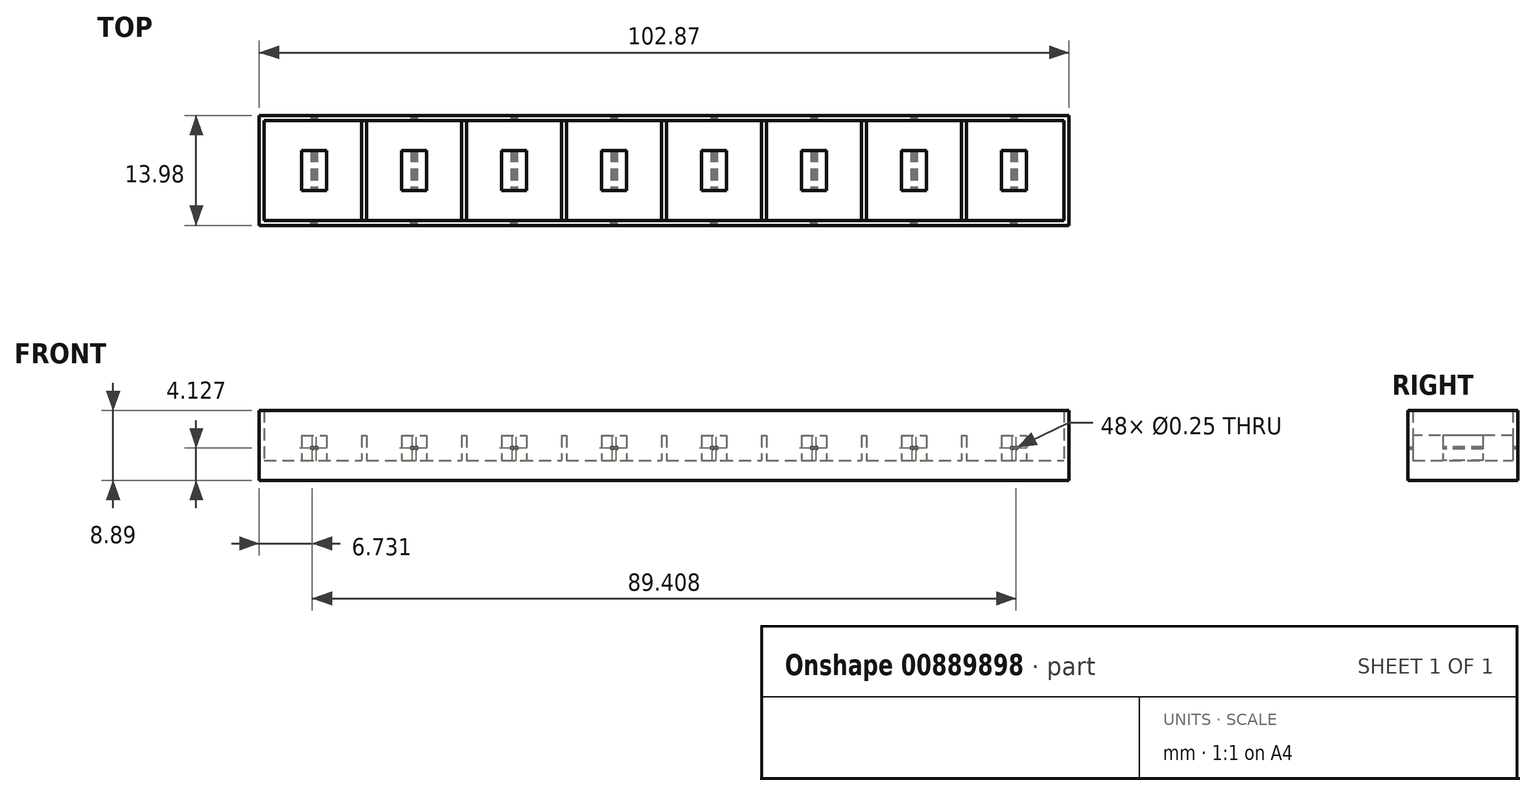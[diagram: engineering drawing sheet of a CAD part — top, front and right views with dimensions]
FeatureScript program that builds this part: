
annotation { "Feature Type Name" : "Feature", "Feature Type Description" : "" }
export const myFeature = defineFeature(function(context is Context, id is Id, definition is map)
    precondition{}
    {
        {
            var Q0;
            Q0=qCreatedBy(makeId("Top.planeOp"),FACE);
            var sketch = newSketch(context, id + "F0", { "sketchPlane" : qUnion([Q0])});
            skLineSegment(sketch, "E0.bottom", {"start": v(-32.74, 0) * mm, "end": v(68.86, 0) * mm});
            skLineSegment(sketch, "E0.top", {"start": v(-32.74, 12.7) * mm, "end": v(68.86, 12.7) * mm});
            skLineSegment(sketch, "E0.left", {"start": v(-32.74, 0) * mm, "end": v(-32.74, 12.7) * mm});
            skLineSegment(sketch, "E0.right", {"start": v(68.86, 0) * mm, "end": v(68.86, 12.7) * mm});
            skLineSegment(sketch, "E1.bottom", {"start": v(69.5, 13.34) * mm, "end": v(-33.37, 13.33) * mm});
            skLineSegment(sketch, "E1.top", {"start": v(69.5, -0.63) * mm, "end": v(-33.37, -0.64) * mm});
            skLineSegment(sketch, "E1.left", {"start": v(69.5, 13.34) * mm, "end": v(69.5, -0.63) * mm});
            skLineSegment(sketch, "E1.right", {"start": v(-33.37, 13.33) * mm, "end": v(-33.37, -0.64) * mm});
            skLineSegment(sketch, "E2.MirrorCS", {"start": v(5.68, 0) * mm, "end": v(5.68, 12.7) * mm});
            skLineSegment(sketch, "E3.MirrorCS", {"start": v(5.04, 0) * mm, "end": v(5.04, 12.7) * mm});
            skLineSegment(sketch, "E4.MirrorCS", {"start": v(-7.02, 0) * mm, "end": v(-7.02, 12.7) * mm});
            skLineSegment(sketch, "E5.MirrorCS", {"start": v(-7.66, 0) * mm, "end": v(-7.66, 12.7) * mm});
            skLineSegment(sketch, "E6.MirrorCS", {"start": v(-19.72, 0) * mm, "end": v(-19.72, 12.7) * mm});
            skLineSegment(sketch, "E7", {"start": v(-20.36, 12.7) * mm, "end": v(-20.36, 0) * mm});
            skLineSegment(sketch, "E8.MirrorCS", {"start": v(30.44, 0) * mm, "end": v(30.44, 12.7) * mm});
            skLineSegment(sketch, "E9.MirrorCS", {"start": v(31.08, 0) * mm, "end": v(31.08, 12.7) * mm});
            skLineSegment(sketch, "E10.MirrorCS", {"start": v(43.14, 0) * mm, "end": v(43.14, 12.7) * mm});
            skLineSegment(sketch, "E11.MirrorCS", {"start": v(43.78, 0) * mm, "end": v(43.78, 12.7) * mm});
            skLineSegment(sketch, "E12.MirrorCS", {"start": v(55.84, 0) * mm, "end": v(55.84, 12.7) * mm});
            skLineSegment(sketch, "E13.MirrorCS", {"start": v(56.48, 12.7) * mm, "end": v(56.48, 0) * mm});
            skLineSegment(sketch, "E14", {"start": v(17.74, 12.7) * mm, "end": v(17.74, 0) * mm});
            skLineSegment(sketch, "E15", {"start": v(18.38, 0) * mm, "end": v(18.38, 12.7) * mm});
            skLineSegment(sketch, "E16.MirrorCS", {"start": v(-24.8, 8.9) * mm, "end": v(-24.8, 3.8) * mm});
            skLineSegment(sketch, "E17.MirrorCS", {"start": v(-27.97, 8.89) * mm, "end": v(-27.97, 3.8) * mm});
            skLineSegment(sketch, "E18", {"start": v(-27.97, 8.89) * mm, "end": v(-24.8, 8.9) * mm});
            skLineSegment(sketch, "E19", {"start": v(-27.97, 3.8) * mm, "end": v(-24.8, 3.8) * mm});
            skLineSegment(sketch, "E20.1.0.0", {"start": v(-15.27, 8.89) * mm, "end": v(-12.1, 8.9) * mm});
            skLineSegment(sketch, "E20.1.0.1", {"start": v(-12.1, 8.9) * mm, "end": v(-12.1, 3.8) * mm});
            skLineSegment(sketch, "E20.1.0.2", {"start": v(-15.27, 8.89) * mm, "end": v(-15.27, 3.8) * mm});
            skLineSegment(sketch, "E20.1.0.3", {"start": v(-15.27, 3.8) * mm, "end": v(-12.1, 3.8) * mm});
            skLineSegment(sketch, "E20.2.0.0", {"start": v(-2.57, 8.89) * mm, "end": v(0.6, 8.9) * mm});
            skLineSegment(sketch, "E20.2.0.1", {"start": v(0.6, 8.9) * mm, "end": v(0.6, 3.8) * mm});
            skLineSegment(sketch, "E20.2.0.2", {"start": v(-2.57, 8.89) * mm, "end": v(-2.57, 3.8) * mm});
            skLineSegment(sketch, "E20.2.0.3", {"start": v(-2.57, 3.8) * mm, "end": v(0.6, 3.8) * mm});
            skLineSegment(sketch, "E20.3.0.0", {"start": v(10.13, 8.89) * mm, "end": v(13.3, 8.9) * mm});
            skLineSegment(sketch, "E20.3.0.1", {"start": v(13.3, 8.9) * mm, "end": v(13.3, 3.8) * mm});
            skLineSegment(sketch, "E20.3.0.2", {"start": v(10.13, 8.89) * mm, "end": v(10.13, 3.8) * mm});
            skLineSegment(sketch, "E20.3.0.3", {"start": v(10.13, 3.8) * mm, "end": v(13.3, 3.8) * mm});
            skLineSegment(sketch, "E20.4.0.0", {"start": v(22.83, 8.89) * mm, "end": v(26, 8.9) * mm});
            skLineSegment(sketch, "E20.4.0.1", {"start": v(26, 8.9) * mm, "end": v(26, 3.8) * mm});
            skLineSegment(sketch, "E20.4.0.2", {"start": v(22.83, 8.89) * mm, "end": v(22.83, 3.8) * mm});
            skLineSegment(sketch, "E20.4.0.3", {"start": v(22.83, 3.8) * mm, "end": v(26, 3.8) * mm});
            skLineSegment(sketch, "E20.5.0.0", {"start": v(35.53, 8.89) * mm, "end": v(38.7, 8.9) * mm});
            skLineSegment(sketch, "E20.5.0.1", {"start": v(38.7, 8.9) * mm, "end": v(38.7, 3.8) * mm});
            skLineSegment(sketch, "E20.5.0.2", {"start": v(35.53, 8.89) * mm, "end": v(35.53, 3.8) * mm});
            skLineSegment(sketch, "E20.5.0.3", {"start": v(35.53, 3.8) * mm, "end": v(38.7, 3.8) * mm});
            skLineSegment(sketch, "E20.6.0.0", {"start": v(48.23, 8.89) * mm, "end": v(51.4, 8.9) * mm});
            skLineSegment(sketch, "E20.6.0.1", {"start": v(51.4, 8.9) * mm, "end": v(51.4, 3.8) * mm});
            skLineSegment(sketch, "E20.6.0.2", {"start": v(48.23, 8.89) * mm, "end": v(48.23, 3.8) * mm});
            skLineSegment(sketch, "E20.6.0.3", {"start": v(48.23, 3.8) * mm, "end": v(51.4, 3.8) * mm});
            skLineSegment(sketch, "E20.7.0.0", {"start": v(60.93, 8.89) * mm, "end": v(64.1, 8.9) * mm});
            skLineSegment(sketch, "E20.7.0.1", {"start": v(64.1, 8.9) * mm, "end": v(64.1, 3.8) * mm});
            skLineSegment(sketch, "E20.7.0.2", {"start": v(60.93, 8.89) * mm, "end": v(60.93, 3.8) * mm});
            skLineSegment(sketch, "E20.7.0.3", {"start": v(60.93, 3.8) * mm, "end": v(64.1, 3.8) * mm});
            skLineSegment(sketch, "E20.direction1", {"start": v(-27.97, 3.8) * mm, "end": v(-15.27, 3.8) * mm, "construction": true});
            skSolve(sketch);
        }
        {
            var Q0;
            {var subQ1=sQuery(id+"F0.wireOp",EDGE,"E5.MirrorCS");Q0=makeQuery(id+"F0.imprint","IMPRINT",FACE,{"disambiguationData":[TD([[makeQuery(id+"F0.imprint","IMPRINT",EDGE,{"derivedFrom":subQ1}),1.0]])]});}
            var Q1;
            {var subQ1=sQuery(id+"F0.wireOp",EDGE,"E3.MirrorCS");Q1=makeQuery(id+"F0.imprint","IMPRINT",FACE,{"disambiguationData":[TD([[makeQuery(id+"F0.imprint","IMPRINT",EDGE,{"derivedFrom":subQ1}),1.0]])]});}
            var Q2;
            {var subQ1=sQuery(id+"F0.wireOp",EDGE,"E0.right");Q2=makeQuery(id+"F0.imprint","IMPRINT",FACE,{"disambiguationData":[TD([[makeQuery(id+"F0.imprint","IMPRINT",EDGE,{"derivedFrom":subQ1}),1.0]])]});}
            var Q3;
            {var subQ1=sQuery(id+"F0.wireOp",EDGE,"E11.MirrorCS");Q3=makeQuery(id+"F0.imprint","IMPRINT",FACE,{"disambiguationData":[TD([[makeQuery(id+"F0.imprint","IMPRINT",EDGE,{"derivedFrom":subQ1}),-1.0]])]});}
            var Q4;
            {var subQ1=sQuery(id+"F0.wireOp",EDGE,"E0.left");Q4=makeQuery(id+"F0.imprint","IMPRINT",FACE,{"disambiguationData":[TD([[makeQuery(id+"F0.imprint","IMPRINT",EDGE,{"derivedFrom":subQ1}),-1.0]])]});}
            var Q5;
            Q5=makeQuery(id+"F0.imprint","IMPRINT",FACE,{"disambiguationData":[TD([[makeQuery(id+"F0.imprint","IMPRINT",EDGE,{"derivedFrom":sQuery(id+"F0.wireOp",EDGE,"E20.6.0.0")}),-1.0]])]});
            var Q6;
            Q6=makeQuery(id+"F0.imprint","IMPRINT",FACE,{"disambiguationData":[TD([[makeQuery(id+"F0.imprint","IMPRINT",EDGE,{"derivedFrom":sQuery(id+"F0.wireOp",EDGE,"E20.4.0.0")}),-1.0]])]});
            var Q7;
            Q7=makeQuery(id+"F0.imprint","IMPRINT",FACE,{"disambiguationData":[TD([[makeQuery(id+"F0.imprint","IMPRINT",EDGE,{"derivedFrom":sQuery(id+"F0.wireOp",EDGE,"E16.MirrorCS")}),-1.0]])]});
            var Q8;
            Q8=makeQuery(id+"F0.imprint","IMPRINT",FACE,{"disambiguationData":[TD([[makeQuery(id+"F0.imprint","IMPRINT",EDGE,{"derivedFrom":sQuery(id+"F0.wireOp",EDGE,"E20.2.0.0")}),-1.0]])]});
            var Q9;
            Q9=makeQuery(id+"F0.imprint","IMPRINT",FACE,{"disambiguationData":[TD([[makeQuery(id+"F0.imprint","IMPRINT",EDGE,{"derivedFrom":sQuery(id+"F0.wireOp",EDGE,"E20.1.0.0")}),-1.0]])]});
            var Q10;
            Q10=makeQuery(id+"F0.imprint","IMPRINT",FACE,{"disambiguationData":[TD([[makeQuery(id+"F0.imprint","IMPRINT",EDGE,{"derivedFrom":sQuery(id+"F0.wireOp",EDGE,"E20.7.0.0")}),-1.0]])]});
            var Q11;
            {var subQ1=sQuery(id+"F0.wireOp",EDGE,"E9.MirrorCS");Q11=makeQuery(id+"F0.imprint","IMPRINT",FACE,{"disambiguationData":[TD([[makeQuery(id+"F0.imprint","IMPRINT",EDGE,{"derivedFrom":subQ1}),-1.0]])]});}
            var Q12;
            Q12=makeQuery(id+"F0.imprint","IMPRINT",FACE,{"disambiguationData":[TD([[makeQuery(id+"F0.imprint","IMPRINT",EDGE,{"derivedFrom":sQuery(id+"F0.wireOp",EDGE,"E20.3.0.0")}),-1.0]])]});
            var Q13;
            {var subQ1=sQuery(id+"F0.wireOp",EDGE,"E2.MirrorCS");Q13=makeQuery(id+"F0.imprint","IMPRINT",FACE,{"disambiguationData":[TD([[makeQuery(id+"F0.imprint","IMPRINT",EDGE,{"derivedFrom":subQ1}),-1.0]])]});}
            var Q14;
            {var subQ1=sQuery(id+"F0.wireOp",EDGE,"E8.MirrorCS");Q14=makeQuery(id+"F0.imprint","IMPRINT",FACE,{"disambiguationData":[TD([[makeQuery(id+"F0.imprint","IMPRINT",EDGE,{"derivedFrom":subQ1}),1.0]])]});}
            var Q15;
            Q15=makeQuery(id+"F0.imprint","IMPRINT",FACE,{"disambiguationData":[TD([[makeQuery(id+"F0.imprint","IMPRINT",EDGE,{"derivedFrom":sQuery(id+"F0.wireOp",EDGE,"E20.5.0.0")}),-1.0]])]});
            var Q16;
            {var subQ15=sQuery(id+"F0.wireOp",EDGE,"E0.left");Q16=makeQuery(id+"F0.imprint","IMPRINT",FACE,{"disambiguationData":[TD([[makeQuery(id+"F0.imprint","IMPRINT",EDGE,{"derivedFrom":subQ15}),1.0]])]});}
            var Q17;
            {var subQ0=sQuery(id+"F0.wireOp",EDGE,"E2.MirrorCS");Q17=makeQuery(id+"F0.imprint","IMPRINT",FACE,{"disambiguationData":[TD([[makeQuery(id+"F0.imprint","IMPRINT",EDGE,{"derivedFrom":subQ0}),1.0]])]});}
            var Q18;
            {var subQ0=sQuery(id+"F0.wireOp",EDGE,"E12.MirrorCS");Q18=makeQuery(id+"F0.imprint","IMPRINT",FACE,{"disambiguationData":[TD([[makeQuery(id+"F0.imprint","IMPRINT",EDGE,{"derivedFrom":subQ0}),-1.0]])]});}
            var Q19;
            {var subQ0=sQuery(id+"F0.wireOp",EDGE,"E14");Q19=makeQuery(id+"F0.imprint","IMPRINT",FACE,{"disambiguationData":[TD([[makeQuery(id+"F0.imprint","IMPRINT",EDGE,{"derivedFrom":subQ0}),1.0]])]});}
            var Q20;
            {var subQ0=sQuery(id+"F0.wireOp",EDGE,"E8.MirrorCS");Q20=makeQuery(id+"F0.imprint","IMPRINT",FACE,{"disambiguationData":[TD([[makeQuery(id+"F0.imprint","IMPRINT",EDGE,{"derivedFrom":subQ0}),-1.0]])]});}
            var Q21;
            {var subQ0=sQuery(id+"F0.wireOp",EDGE,"E10.MirrorCS");Q21=makeQuery(id+"F0.imprint","IMPRINT",FACE,{"disambiguationData":[TD([[makeQuery(id+"F0.imprint","IMPRINT",EDGE,{"derivedFrom":subQ0}),-1.0]])]});}
            var Q22;
            {var subQ0=sQuery(id+"F0.wireOp",EDGE,"E4.MirrorCS");Q22=makeQuery(id+"F0.imprint","IMPRINT",FACE,{"disambiguationData":[TD([[makeQuery(id+"F0.imprint","IMPRINT",EDGE,{"derivedFrom":subQ0}),1.0]])]});}
            var Q23;
            {var subQ0=sQuery(id+"F0.wireOp",EDGE,"E6.MirrorCS");Q23=makeQuery(id+"F0.imprint","IMPRINT",FACE,{"disambiguationData":[TD([[makeQuery(id+"F0.imprint","IMPRINT",EDGE,{"derivedFrom":subQ0}),1.0]])]});}
            extrude(context, id + "F1", {"entities" : qUnion([Q0, Q1, Q2, Q3, Q4, Q5, Q6, Q7, Q8, Q9, Q10, Q11, Q12, Q13, Q14, Q15, Q16, Q17, Q18, Q19, Q20, Q21, Q22, Q23]), "oppositeDirection" : true, "depth" : 2.54 * mm, "offsetDistance" : 25.4 * mm});
        }
        {
            var Q0;
            {var subQ19=sQuery(id+"F0.wireOp",EDGE,"E0.left");Q0=makeQuery(id+"F0.imprint","IMPRINT",FACE,{"disambiguationData":[TD([[makeQuery(id+"F0.imprint","IMPRINT",EDGE,{"derivedFrom":subQ19}),1.0]])]});}
            extrude(context, id + "F2", {"entities" : qUnion([Q0]), "operationType" : NewBodyOperationType.ADD, "depth" : 6.35 * mm, "offsetDistance" : 25.4 * mm});
        }
        {
            var Q0;
            Q0=makeQuery(id+"F0.imprint","IMPRINT",FACE,{"disambiguationData":[TD([[makeQuery(id+"F0.imprint","IMPRINT",EDGE,{"derivedFrom":sQuery(id+"F0.wireOp",EDGE,"E16.MirrorCS")}),-1.0]])]});
            var Q1;
            Q1=makeQuery(id+"F0.imprint","IMPRINT",FACE,{"disambiguationData":[TD([[makeQuery(id+"F0.imprint","IMPRINT",EDGE,{"derivedFrom":sQuery(id+"F0.wireOp",EDGE,"E20.1.0.0")}),-1.0]])]});
            var Q2;
            Q2=makeQuery(id+"F0.imprint","IMPRINT",FACE,{"disambiguationData":[TD([[makeQuery(id+"F0.imprint","IMPRINT",EDGE,{"derivedFrom":sQuery(id+"F0.wireOp",EDGE,"E20.2.0.0")}),-1.0]])]});
            var Q3;
            Q3=makeQuery(id+"F0.imprint","IMPRINT",FACE,{"disambiguationData":[TD([[makeQuery(id+"F0.imprint","IMPRINT",EDGE,{"derivedFrom":sQuery(id+"F0.wireOp",EDGE,"E20.3.0.0")}),-1.0]])]});
            var Q4;
            Q4=makeQuery(id+"F0.imprint","IMPRINT",FACE,{"disambiguationData":[TD([[makeQuery(id+"F0.imprint","IMPRINT",EDGE,{"derivedFrom":sQuery(id+"F0.wireOp",EDGE,"E20.4.0.0")}),-1.0]])]});
            var Q5;
            Q5=makeQuery(id+"F0.imprint","IMPRINT",FACE,{"disambiguationData":[TD([[makeQuery(id+"F0.imprint","IMPRINT",EDGE,{"derivedFrom":sQuery(id+"F0.wireOp",EDGE,"E20.5.0.0")}),-1.0]])]});
            var Q6;
            Q6=makeQuery(id+"F0.imprint","IMPRINT",FACE,{"disambiguationData":[TD([[makeQuery(id+"F0.imprint","IMPRINT",EDGE,{"derivedFrom":sQuery(id+"F0.wireOp",EDGE,"E20.6.0.0")}),-1.0]])]});
            var Q7;
            Q7=makeQuery(id+"F0.imprint","IMPRINT",FACE,{"disambiguationData":[TD([[makeQuery(id+"F0.imprint","IMPRINT",EDGE,{"derivedFrom":sQuery(id+"F0.wireOp",EDGE,"E20.7.0.0")}),-1.0]])]});
            var Q8;
            {var subQ0=sQuery(id+"F0.wireOp",EDGE,"E12.MirrorCS");Q8=makeQuery(id+"F0.imprint","IMPRINT",FACE,{"disambiguationData":[TD([[makeQuery(id+"F0.imprint","IMPRINT",EDGE,{"derivedFrom":subQ0}),-1.0]])]});}
            var Q9;
            {var subQ0=sQuery(id+"F0.wireOp",EDGE,"E10.MirrorCS");Q9=makeQuery(id+"F0.imprint","IMPRINT",FACE,{"disambiguationData":[TD([[makeQuery(id+"F0.imprint","IMPRINT",EDGE,{"derivedFrom":subQ0}),-1.0]])]});}
            var Q10;
            {var subQ0=sQuery(id+"F0.wireOp",EDGE,"E8.MirrorCS");Q10=makeQuery(id+"F0.imprint","IMPRINT",FACE,{"disambiguationData":[TD([[makeQuery(id+"F0.imprint","IMPRINT",EDGE,{"derivedFrom":subQ0}),-1.0]])]});}
            var Q11;
            {var subQ0=sQuery(id+"F0.wireOp",EDGE,"E14");Q11=makeQuery(id+"F0.imprint","IMPRINT",FACE,{"disambiguationData":[TD([[makeQuery(id+"F0.imprint","IMPRINT",EDGE,{"derivedFrom":subQ0}),1.0]])]});}
            var Q12;
            {var subQ0=sQuery(id+"F0.wireOp",EDGE,"E2.MirrorCS");Q12=makeQuery(id+"F0.imprint","IMPRINT",FACE,{"disambiguationData":[TD([[makeQuery(id+"F0.imprint","IMPRINT",EDGE,{"derivedFrom":subQ0}),1.0]])]});}
            var Q13;
            {var subQ0=sQuery(id+"F0.wireOp",EDGE,"E4.MirrorCS");Q13=makeQuery(id+"F0.imprint","IMPRINT",FACE,{"disambiguationData":[TD([[makeQuery(id+"F0.imprint","IMPRINT",EDGE,{"derivedFrom":subQ0}),1.0]])]});}
            var Q14;
            {var subQ0=sQuery(id+"F0.wireOp",EDGE,"E6.MirrorCS");Q14=makeQuery(id+"F0.imprint","IMPRINT",FACE,{"disambiguationData":[TD([[makeQuery(id+"F0.imprint","IMPRINT",EDGE,{"derivedFrom":subQ0}),1.0]])]});}
            extrude(context, id + "F3", {"entities" : qUnion([Q0, Q1, Q2, Q3, Q4, Q5, Q6, Q7, Q8, Q9, Q10, Q11, Q12, Q13, Q14]), "operationType" : NewBodyOperationType.ADD, "depth" : 3.17 * mm, "offsetDistance" : 25.4 * mm});
        }
        {
            var Q0;
            Q0=makeQuery(id+"F2.opExtrude","SWEPT_FACE",FACE,{"disambiguationData":[OSD([sQuery(id+"F0.wireOp",EDGE,"E0.bottom"),sQuery(id+"F0.wireOp",EDGE,"Ld5J9Fpd-gWnr-y3Wp-gADY-ncH7xOH5REKi.bottom")])]});
            var sketch = newSketch(context, id + "F4", { "sketchPlane" : qUnion([Q0])});
            skPoint(sketch, "E21", {"position": v(-24.67, 1.59) * mm});
            skPoint(sketch, "E22", {"position": v(-24.16, 1.59) * mm});
            skPoint(sketch, "E23.MirrorP", {"position": v(-36.86, 1.59) * mm});
            skPoint(sketch, "E24.MirrorP", {"position": v(-37.37, 1.59) * mm});
            skPoint(sketch, "E25.MirrorP", {"position": v(-49.56, 1.59) * mm});
            skPoint(sketch, "E26.MirrorP", {"position": v(-50.07, 1.59) * mm});
            skPoint(sketch, "E27.MirrorP", {"position": v(-62.26, 1.59) * mm});
            skPoint(sketch, "E28.MirrorP", {"position": v(-62.77, 1.59) * mm});
            skPoint(sketch, "E29.MirrorP", {"position": v(-11.97, 1.59) * mm});
            skPoint(sketch, "E30.MirrorP", {"position": v(-11.46, 1.59) * mm});
            skPoint(sketch, "E31.MirrorP", {"position": v(0.73, 1.59) * mm});
            skPoint(sketch, "E32.MirrorP", {"position": v(1.24, 1.59) * mm});
            skPoint(sketch, "E33.MirrorP", {"position": v(13.43, 1.59) * mm});
            skPoint(sketch, "E34.MirrorP", {"position": v(13.94, 1.59) * mm});
            skPoint(sketch, "E35.MirrorP", {"position": v(26.13, 1.59) * mm});
            skPoint(sketch, "E36.MirrorP", {"position": v(26.64, 1.59) * mm});
            skSolve(sketch);
        }
        {
            var Q0;
            Q0=sQuery(id+"F4.wireOp",VERTEX,"E36.MirrorP");
            var Q1;
            Q1=sQuery(id+"F4.wireOp",VERTEX,"E35.MirrorP");
            var Q2;
            Q2=sQuery(id+"F4.wireOp",VERTEX,"E34.MirrorP");
            var Q3;
            Q3=sQuery(id+"F4.wireOp",VERTEX,"E33.MirrorP");
            var Q4;
            Q4=sQuery(id+"F4.wireOp",VERTEX,"E32.MirrorP");
            var Q5;
            Q5=sQuery(id+"F4.wireOp",VERTEX,"E31.MirrorP");
            var Q6;
            Q6=sQuery(id+"F4.wireOp",VERTEX,"E30.MirrorP");
            var Q7;
            Q7=sQuery(id+"F4.wireOp",VERTEX,"E29.MirrorP");
            var Q8;
            Q8=sQuery(id+"F4.wireOp",VERTEX,"E22");
            var Q9;
            Q9=sQuery(id+"F4.wireOp",VERTEX,"E21");
            var Q10;
            Q10=sQuery(id+"F4.wireOp",VERTEX,"E23.MirrorP");
            var Q11;
            Q11=sQuery(id+"F4.wireOp",VERTEX,"E24.MirrorP");
            var Q12;
            Q12=sQuery(id+"F4.wireOp",VERTEX,"E25.MirrorP");
            var Q13;
            Q13=sQuery(id+"F4.wireOp",VERTEX,"E26.MirrorP");
            var Q14;
            Q14=sQuery(id+"F4.wireOp",VERTEX,"E27.MirrorP");
            var Q15;
            Q15=sQuery(id+"F4.wireOp",VERTEX,"E28.MirrorP");
            var Q16;
            Q16=makeQuery(id+"F1.opExtrude","SWEPT_BODY",BODY,{"disambiguationData":[OSD([sQuery(id+"F0.wireOp",EDGE,"E1.bottom"),sQuery(id+"F0.wireOp",EDGE,"E1.top"),sQuery(id+"F0.wireOp",EDGE,"E1.left"),sQuery(id+"F0.wireOp",EDGE,"E1.right")])]});
            hole(context, id + "F5", {"style" : HoleStyle.SIMPLE, "endStyle" : HoleEndStyle.THROUGH, "holeDiameter" : 0.25 * mm, "majorDiameter" : 6.35 * mm, "isTappedThrough" : true, "tappedDepth" : 12.7 * mm, "tapClearance" : 3, "locations" : qUnion([Q0, Q1, Q2, Q3, Q4, Q5, Q6, Q7, Q8, Q9, Q10, Q11, Q12, Q13, Q14, Q15]), "scope" : qUnion([Q16])});
        }
        {
            var Q0;
            Q0=sQuery(id+"F4.wireOp",VERTEX,"E28.MirrorP");
            var Q1;
            Q1=sQuery(id+"F4.wireOp",VERTEX,"E27.MirrorP");
            var Q2;
            Q2=sQuery(id+"F4.wireOp",VERTEX,"E26.MirrorP");
            var Q3;
            Q3=sQuery(id+"F4.wireOp",VERTEX,"E25.MirrorP");
            var Q4;
            Q4=sQuery(id+"F4.wireOp",VERTEX,"E24.MirrorP");
            var Q5;
            Q5=sQuery(id+"F4.wireOp",VERTEX,"E23.MirrorP");
            var Q6;
            Q6=sQuery(id+"F4.wireOp",VERTEX,"E21");
            var Q7;
            Q7=sQuery(id+"F4.wireOp",VERTEX,"E22");
            var Q8;
            Q8=sQuery(id+"F4.wireOp",VERTEX,"E29.MirrorP");
            var Q9;
            Q9=sQuery(id+"F4.wireOp",VERTEX,"E30.MirrorP");
            var Q10;
            Q10=sQuery(id+"F4.wireOp",VERTEX,"E31.MirrorP");
            var Q11;
            Q11=sQuery(id+"F4.wireOp",VERTEX,"E32.MirrorP");
            var Q12;
            Q12=sQuery(id+"F4.wireOp",VERTEX,"E33.MirrorP");
            var Q13;
            Q13=sQuery(id+"F4.wireOp",VERTEX,"E34.MirrorP");
            var Q14;
            Q14=sQuery(id+"F4.wireOp",VERTEX,"E35.MirrorP");
            var Q15;
            Q15=sQuery(id+"F4.wireOp",VERTEX,"E36.MirrorP");
            var Q16;
            Q16=makeQuery(id+"F1.opExtrude","SWEPT_BODY",BODY,{"disambiguationData":[OSD([sQuery(id+"F0.wireOp",EDGE,"E1.bottom"),sQuery(id+"F0.wireOp",EDGE,"E1.top"),sQuery(id+"F0.wireOp",EDGE,"E1.left"),sQuery(id+"F0.wireOp",EDGE,"E1.right")])]});
            hole(context, id + "F6", {"style" : HoleStyle.SIMPLE, "endStyle" : HoleEndStyle.THROUGH, "oppositeDirection" : true, "holeDiameter" : 0.25 * mm, "majorDiameter" : 6.35 * mm, "isTappedThrough" : true, "tappedDepth" : 12.7 * mm, "tapClearance" : 3, "locations" : qUnion([Q0, Q1, Q2, Q3, Q4, Q5, Q6, Q7, Q8, Q9, Q10, Q11, Q12, Q13, Q14, Q15]), "scope" : qUnion([Q16])});
        }
    });
